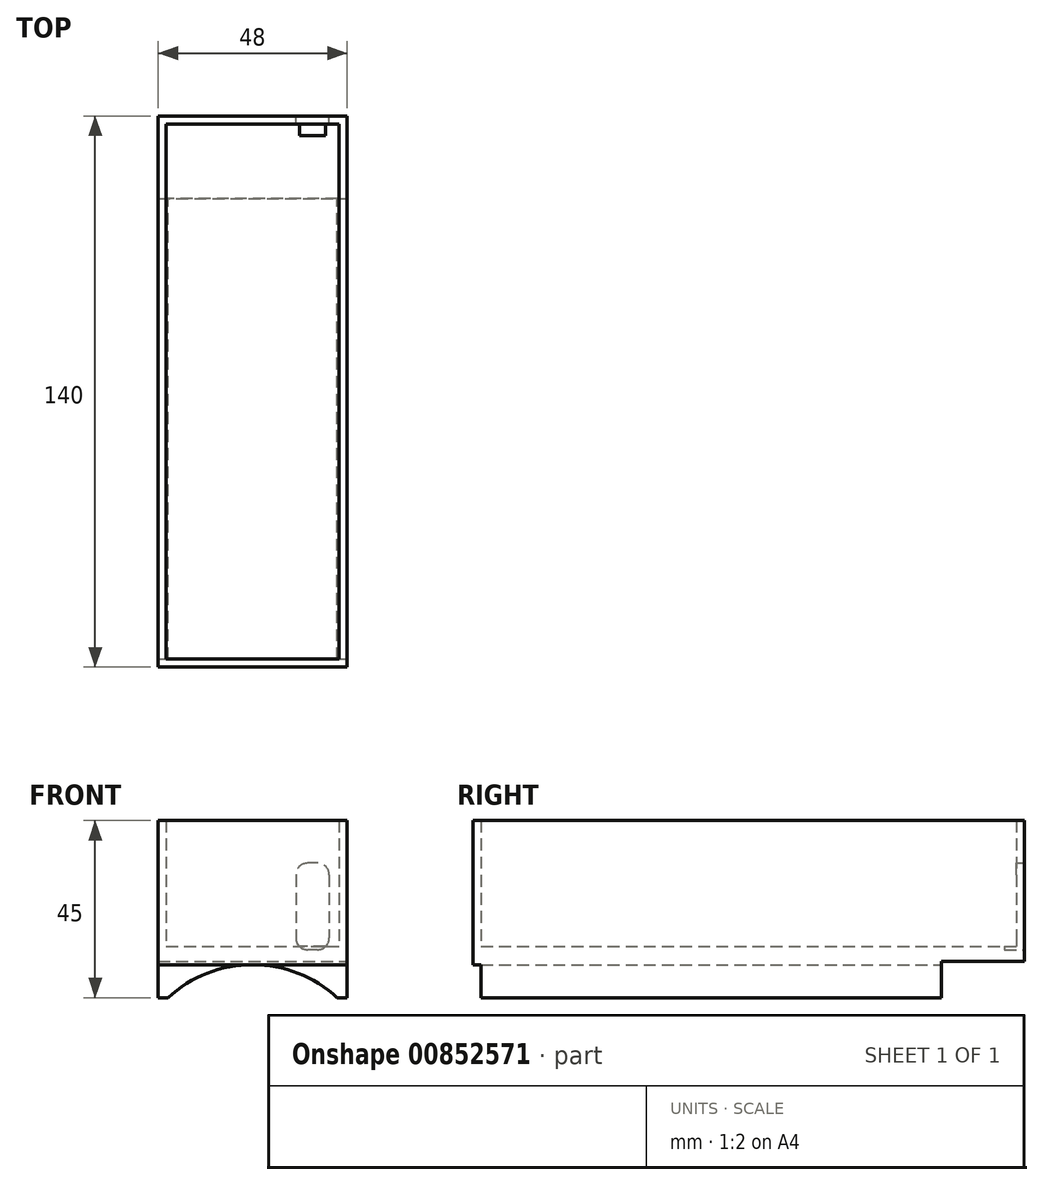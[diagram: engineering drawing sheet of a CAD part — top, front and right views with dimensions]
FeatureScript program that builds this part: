
annotation { "Feature Type Name" : "Feature", "Feature Type Description" : "" }
export const myFeature = defineFeature(function(context is Context, id is Id, definition is map)
    precondition{}
    {
        {
            var Q0;
            Q0=qCreatedBy(makeId("Front.planeOp"),FACE);
            var sketch = newSketch(context, id + "F0", { "sketchPlane" : qUnion([Q0])});
            skArc(sketch, "E0", {"start": v(21.5, 23.36) * mm, "mid": v(0, 31.75) * mm, "end": v(-21.5, 23.36) * mm});
            skLineSegment(sketch, "E1", {"start": v(22, 68.36) * mm, "end": v(22, 36.36) * mm});
            skLineSegment(sketch, "E2", {"start": v(22, 68.36) * mm, "end": v(24, 68.36) * mm});
            skLineSegment(sketch, "E3", {"start": v(24, 68.36) * mm, "end": v(24, 23.36) * mm});
            skLineSegment(sketch, "E4", {"start": v(-22, 68.36) * mm, "end": v(-24, 68.36) * mm});
            skLineSegment(sketch, "E5", {"start": v(-24, 68.36) * mm, "end": v(-24, 23.36) * mm});
            skLineSegment(sketch, "E6", {"start": v(-24, 23.36) * mm, "end": v(-21.5, 23.36) * mm});
            skLineSegment(sketch, "E7.trimOffspring", {"start": v(21.5, 23.36) * mm, "end": v(24, 23.36) * mm});
            skLineSegment(sketch, "E8", {"start": v(-22, 36.36) * mm, "end": v(22, 36.36) * mm});
            skPoint(sketch, "E9.start.orphan", {"position": v(0, 31.75) * mm});
            skPoint(sketch, "E10.orphan", {"position": v(22, 32.46) * mm});
            skLineSegment(sketch, "E11", {"start": v(-22, 68.36) * mm, "end": v(-22, 36.36) * mm});
            skArc(sketch, "E12", {"start": v(24, 24.08) * mm, "mid": v(0, 34) * mm, "end": v(-24, 24.08) * mm});
            skArc(sketch, "E13", {"start": v(24, 26.83) * mm, "mid": v(0, 36) * mm, "end": v(-24, 26.83) * mm});
            skSolve(sketch);
        }
        {
            var Q0;
            Q0=makeQuery(id+"F0.imprint","IMPRINT",FACE,{"disambiguationData":[TD([[makeQuery(id+"F0.imprint","IMPRINT",EDGE,{"derivedFrom":sQuery(id+"F0.wireOp",EDGE,"E1")}),1.0]])]});
            var Q1;
            {var subQ0=sQuery(id+"F0.wireOp",EDGE,"E12");Q1=makeQuery(id+"F0.imprint","IMPRINT",FACE,{"disambiguationData":[TD([[makeQuery(id+"F0.imprint","IMPRINT",EDGE,{"derivedFrom":subQ0}),-1.0]])]});}
            var Q2;
            Q2=makeQuery(id+"F0.imprint","IMPRINT",FACE,{"disambiguationData":[TD([[makeQuery(id+"F0.imprint","IMPRINT",EDGE,{"derivedFrom":sQuery(id+"F0.wireOp",EDGE,"E0")}),-1.0]])]});
            extrude(context, id + "F1", {"entities" : qUnion([Q0, Q1, Q2]), "depth" : 117 * mm, "offsetDistance" : 25 * mm});
        }
        {
            var Q0;
            Q0=makeQuery(id+"F1.opExtrude","CAP_FACE",FACE,{"disambiguationData":[OSD([sQuery(id+"F0.wireOp",EDGE,"E0"),sQuery(id+"F0.wireOp",EDGE,"E1"),sQuery(id+"F0.wireOp",EDGE,"E2"),sQuery(id+"F0.wireOp",EDGE,"E3"),sQuery(id+"F0.wireOp",EDGE,"E4"),sQuery(id+"F0.wireOp",EDGE,"E5"),sQuery(id+"F0.wireOp",EDGE,"E6"),sQuery(id+"F0.wireOp",EDGE,"E7.trimOffspring"),sQuery(id+"F0.wireOp",EDGE,"E8"),sQuery(id+"F0.wireOp",EDGE,"E11")])],"isStart":true});
            var sketch = newSketch(context, id + "F2", { "sketchPlane" : qUnion([Q0])});
            skLineSegment(sketch, "E14", {"start": v(0, 32.54) * mm, "end": v(24, 32.54) * mm});
            skLineSegment(sketch, "E15", {"start": v(0, 32.54) * mm, "end": v(-24, 32.54) * mm});
            skPoint(sketch, "E16.start.orphan", {"position": v(0, 36.36) * mm});
            skSolve(sketch);
        }
        {
            var Q0;
            {var subQ4=sQuery(id+"F2.wireOp",EDGE,"E14");Q0=makeQuery(id+"F2.imprint","IMPRINT",FACE,{"disambiguationData":[TD([[makeQuery(id+"F2.imprint","IMPRINT",EDGE,{"derivedFrom":subQ4}),1.0]])]});}
            extrude(context, id + "F3", {"entities" : qUnion([Q0]), "operationType" : NewBodyOperationType.ADD, "depth" : 19 * mm, "offsetDistance" : 25 * mm});
        }
        {
            var Q0;
            Q0=makeQuery(id+"F3.opExtrude","CAP_FACE",FACE,{"disambiguationData":[OSD([sQuery(id+"F0.wireOp",EDGE,"E1"),sQuery(id+"F0.wireOp",EDGE,"E2"),sQuery(id+"F0.wireOp",EDGE,"E3"),sQuery(id+"F0.wireOp",EDGE,"E4"),sQuery(id+"F0.wireOp",EDGE,"E5"),sQuery(id+"F0.wireOp",EDGE,"E8"),sQuery(id+"F0.wireOp",EDGE,"E11"),sQuery(id+"F2.wireOp",EDGE,"E14"),sQuery(id+"F2.wireOp",EDGE,"E15")])],"isStart":false});
            var sketch = newSketch(context, id + "F4", { "sketchPlane" : qUnion([Q0])});
            skLineSegment(sketch, "E17", {"start": v(-24, 68.36) * mm, "end": v(24, 68.36) * mm});
            skLineSegment(sketch, "E18", {"start": v(24, 68.36) * mm, "end": v(24, 32.54) * mm});
            skLineSegment(sketch, "E19", {"start": v(24, 32.54) * mm, "end": v(-24, 32.54) * mm});
            skLineSegment(sketch, "E20", {"start": v(-24, 32.54) * mm, "end": v(-24, 68.36) * mm});
            skSolve(sketch);
        }
        {
            var Q0;
            Q0 = qSketchRegion(id + "F4", true);
            extrude(context, id + "F5", {"entities" : qUnion([Q0]), "operationType" : NewBodyOperationType.ADD, "depth" : 2 * mm, "offsetDistance" : 25 * mm});
        }
        {
            var Q0;
            Q0=makeQuery(id+"F1.opExtrude","CAP_FACE",FACE,{"disambiguationData":[OSD([sQuery(id+"F0.wireOp",EDGE,"E0"),sQuery(id+"F0.wireOp",EDGE,"E1"),sQuery(id+"F0.wireOp",EDGE,"E2"),sQuery(id+"F0.wireOp",EDGE,"E3"),sQuery(id+"F0.wireOp",EDGE,"E4"),sQuery(id+"F0.wireOp",EDGE,"E5"),sQuery(id+"F0.wireOp",EDGE,"E6"),sQuery(id+"F0.wireOp",EDGE,"E7.trimOffspring"),sQuery(id+"F0.wireOp",EDGE,"E8"),sQuery(id+"F0.wireOp",EDGE,"E11")])],"isStart":false});
            var sketch = newSketch(context, id + "F6", { "sketchPlane" : qUnion([Q0])});
            skLineSegment(sketch, "E21", {"start": v(-24, 68.36) * mm, "end": v(24, 68.36) * mm});
            skLineSegment(sketch, "E22", {"start": v(0, 31.75) * mm, "end": v(-24, 31.75) * mm});
            skLineSegment(sketch, "E23", {"start": v(-24, 31.75) * mm, "end": v(-24, 68.36) * mm});
            skLineSegment(sketch, "E24", {"start": v(0, 31.75) * mm, "end": v(24, 31.75) * mm});
            skLineSegment(sketch, "E25", {"start": v(24, 31.75) * mm, "end": v(24, 68.36) * mm});
            skSolve(sketch);
        }
        {
            var Q0;
            {var subQ1=makeQuery(id+"F1.opExtrude","CAP_EDGE",EDGE,{"disambiguationData":[OSD([sQuery(id+"F0.wireOp",EDGE,"E1")])],"isStart":false});Q0=makeQuery(id+"F6.imprint","IMPRINT",FACE,{"disambiguationData":[TD([[makeQuery(id+"F6.imprint","IMPRINT",EDGE,{"derivedFrom":subQ1}),-1.0]])]});}
            var Q1;
            Q1=makeQuery(id+"F6.imprint","IMPRINT",FACE,{"disambiguationData":[TD([[makeQuery(id+"F6.imprint","IMPRINT",EDGE,{"derivedFrom":sQuery(id+"F6.wireOp",EDGE,"E22")}),-1.0]])]});
            extrude(context, id + "F7", {"entities" : qUnion([Q0, Q1]), "operationType" : NewBodyOperationType.ADD, "depth" : 2 * mm, "offsetDistance" : 25 * mm});
        }
        {
            var Q0;
            Q0=makeQuery(id+"F5.opExtrude","CAP_FACE",FACE,{"disambiguationData":[OSD([sQuery(id+"F4.wireOp",EDGE,"E17"),sQuery(id+"F4.wireOp",EDGE,"E18"),sQuery(id+"F4.wireOp",EDGE,"E19"),sQuery(id+"F4.wireOp",EDGE,"E20")])],"isStart":false});
            var sketch = newSketch(context, id + "F8", { "sketchPlane" : qUnion([Q0])});
            skLineSegment(sketch, "E26.bottom", {"start": v(-16.46, 57.54) * mm, "end": v(-13.96, 57.54) * mm});
            skLineSegment(sketch, "E26.top", {"start": v(-16.46, 35.54) * mm, "end": v(-13.96, 35.54) * mm});
            skLineSegment(sketch, "E26.left", {"start": v(-19.46, 54.54) * mm, "end": v(-19.46, 38.54) * mm});
            skLineSegment(sketch, "E26.right", {"start": v(-10.96, 54.54) * mm, "end": v(-10.96, 38.54) * mm});
            skLineSegment(sketch, "E27", {"start": v(-15.2, 35.54) * mm, "end": v(-15.2, 32.54) * mm});
            skPoint(sketch, "E28.visualSharp", {"position": v(-19.46, 35.54) * mm});
            skArc(sketch, "E28.filletArc", {"start": v(-19.46, 38.54) * mm, "mid": v(-18.58, 36.42) * mm, "end": v(-16.46, 35.54) * mm});
            skPoint(sketch, "E29.visualSharp", {"position": v(-10.96, 35.54) * mm});
            skArc(sketch, "E29.filletArc", {"start": v(-13.96, 35.54) * mm, "mid": v(-11.84, 36.42) * mm, "end": v(-10.96, 38.54) * mm});
            skPoint(sketch, "E30.visualSharp", {"position": v(-19.46, 57.54) * mm});
            skArc(sketch, "E30.filletArc", {"start": v(-16.46, 57.54) * mm, "mid": v(-18.58, 56.67) * mm, "end": v(-19.46, 54.54) * mm});
            skPoint(sketch, "E31.visualSharp", {"position": v(-10.96, 57.54) * mm});
            skArc(sketch, "E31.filletArc", {"start": v(-10.96, 54.54) * mm, "mid": v(-11.84, 56.67) * mm, "end": v(-13.96, 57.54) * mm});
            skSolve(sketch);
        }
        {
            var Q0;
            Q0=makeQuery(id+"F8.imprint","IMPRINT",FACE,{"disambiguationData":[TD([[makeQuery(id+"F8.imprint","IMPRINT",EDGE,{"derivedFrom":sQuery(id+"F8.wireOp",EDGE,"E26.bottom")}),-1.0]])]});
            extrude(context, id + "F9", {"entities" : qUnion([Q0]), "operationType" : NewBodyOperationType.REMOVE, "oppositeDirection" : true, "depth" : 5 * mm, "offsetDistance" : 25 * mm});
        }
    });
